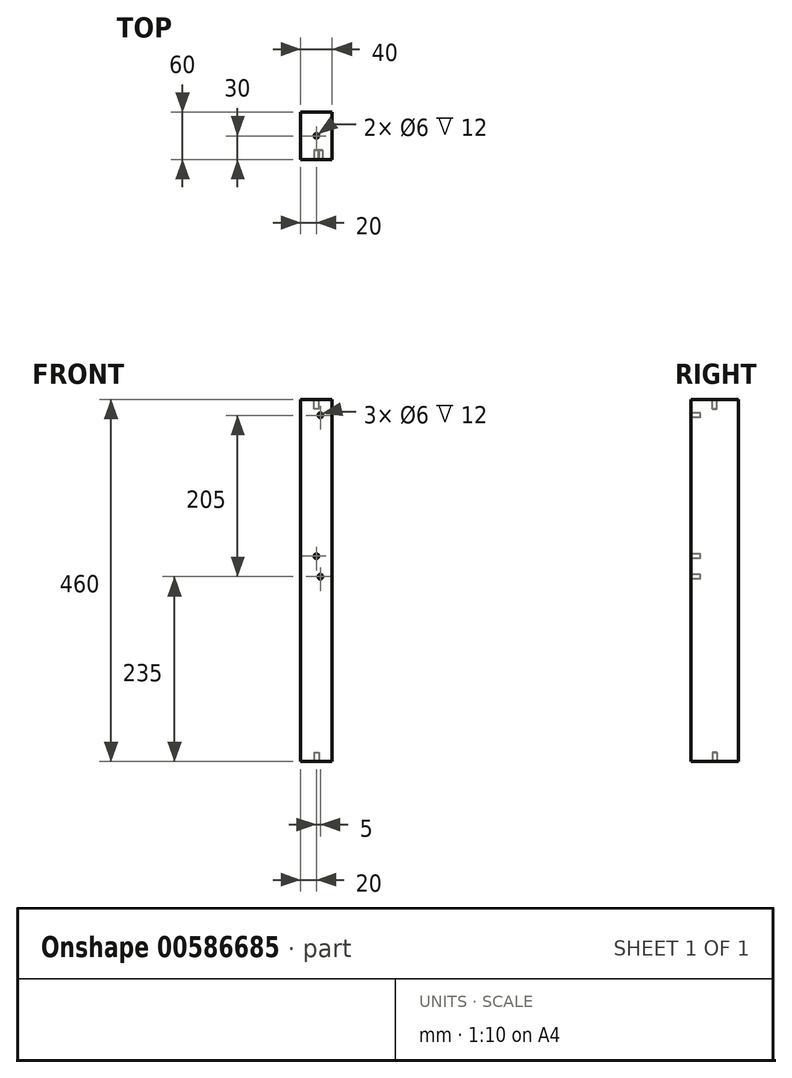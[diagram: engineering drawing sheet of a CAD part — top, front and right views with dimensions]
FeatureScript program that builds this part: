
annotation { "Feature Type Name" : "Feature", "Feature Type Description" : "" }
export const myFeature = defineFeature(function(context is Context, id is Id, definition is map)
    precondition{}
    {
        {
            var Q0;
            Q0=qCreatedBy(makeId("Top.planeOp"),FACE);
            var sketch = newSketch(context, id + "F0", { "sketchPlane" : qUnion([Q0])});
            skLineSegment(sketch, "E0.bottom", {"start": v(0, 0) * mm, "end": v(40, 0) * mm});
            skLineSegment(sketch, "E0.top", {"start": v(0, 60) * mm, "end": v(40, 60) * mm});
            skLineSegment(sketch, "E0.left", {"start": v(0, 0) * mm, "end": v(0, 60) * mm});
            skLineSegment(sketch, "E0.right", {"start": v(40, 0) * mm, "end": v(40, 60) * mm});
            skSolve(sketch);
        }
        {
            var Q0;
            Q0 = qSketchRegion(id + "F0", true);
            extrude(context, id + "F1", {"entities" : qUnion([Q0]), "depth" : 460 * mm, "offsetDistance" : 25 * mm});
        }
        {
            var Q0;
            Q0=makeQuery(id+"F1.opExtrude","CAP_FACE",FACE,{"disambiguationData":[OSD([sQuery(id+"F0.wireOp",EDGE,"E0.bottom"),sQuery(id+"F0.wireOp",EDGE,"E0.top"),sQuery(id+"F0.wireOp",EDGE,"E0.left"),sQuery(id+"F0.wireOp",EDGE,"E0.right")])],"isStart":true});
            var sketch = newSketch(context, id + "F2", { "sketchPlane" : qUnion([Q0])});
            skCircle(sketch, "E1", {"center": v(20, -30) * mm, "radius": 3 * mm});
            skSolve(sketch);
        }
        {
            var Q0;
            Q0 = qSketchRegion(id + "F2", true);
            extrude(context, id + "F3", {"entities" : qUnion([Q0]), "operationType" : NewBodyOperationType.REMOVE, "oppositeDirection" : true, "depth" : 12 * mm, "offsetDistance" : 25 * mm});
        }
        {
            var Q0;
            Q0=makeQuery(id+"F1.opExtrude","CAP_FACE",FACE,{"disambiguationData":[OSD([sQuery(id+"F0.wireOp",EDGE,"E0.bottom"),sQuery(id+"F0.wireOp",EDGE,"E0.top"),sQuery(id+"F0.wireOp",EDGE,"E0.left"),sQuery(id+"F0.wireOp",EDGE,"E0.right")])],"isStart":false});
            var sketch = newSketch(context, id + "F4", { "sketchPlane" : qUnion([Q0])});
            skCircle(sketch, "E2.0", {"center": v(20, 30) * mm, "radius": 3 * mm});
            skSolve(sketch);
        }
        {
            var Q0;
            Q0 = qSketchRegion(id + "F4", true);
            extrude(context, id + "F5", {"entities" : qUnion([Q0]), "operationType" : NewBodyOperationType.REMOVE, "oppositeDirection" : true, "depth" : 12 * mm, "offsetDistance" : 25 * mm});
        }
        {
            var Q0;
            Q0=makeQuery(id+"F1.opExtrude","SWEPT_FACE",FACE,{"disambiguationData":[OSD([sQuery(id+"F0.wireOp",EDGE,"E0.bottom")])]});
            var sketch = newSketch(context, id + "F6", { "sketchPlane" : qUnion([Q0])});
            skCircle(sketch, "E3", {"center": v(20, 261) * mm, "radius": 3 * mm});
            skSolve(sketch);
        }
        {
            var Q0;
            Q0 = qSketchRegion(id + "F6", true);
            extrude(context, id + "F7", {"entities" : qUnion([Q0]), "operationType" : NewBodyOperationType.REMOVE, "oppositeDirection" : true, "depth" : 12 * mm, "offsetDistance" : 25 * mm});
        }
        {
            var Q0;
            Q0=makeQuery(id+"F1.opExtrude","SWEPT_FACE",FACE,{"disambiguationData":[OSD([sQuery(id+"F0.wireOp",EDGE,"E0.bottom")])]});
            var sketch = newSketch(context, id + "F8", { "sketchPlane" : qUnion([Q0])});
            skCircle(sketch, "E4", {"center": v(25, 440) * mm, "radius": 3 * mm});
            skSolve(sketch);
        }
        {
            var Q0;
            Q0 = qSketchRegion(id + "F8", true);
            extrude(context, id + "F9", {"entities" : qUnion([Q0]), "operationType" : NewBodyOperationType.REMOVE, "oppositeDirection" : true, "depth" : 12 * mm, "offsetDistance" : 25 * mm});
        }
        {
            var Q0;
            Q0=makeQuery(id+"F1.opExtrude","SWEPT_FACE",FACE,{"disambiguationData":[OSD([sQuery(id+"F0.wireOp",EDGE,"E0.bottom")])]});
            var sketch = newSketch(context, id + "F10", { "sketchPlane" : qUnion([Q0])});
            skCircle(sketch, "E5", {"center": v(25, 235) * mm, "radius": 3 * mm});
            skSolve(sketch);
        }
        {
            var Q0;
            Q0 = qSketchRegion(id + "F10", true);
            extrude(context, id + "F11", {"entities" : qUnion([Q0]), "operationType" : NewBodyOperationType.REMOVE, "oppositeDirection" : true, "depth" : 12 * mm, "offsetDistance" : 25 * mm});
        }
    });
